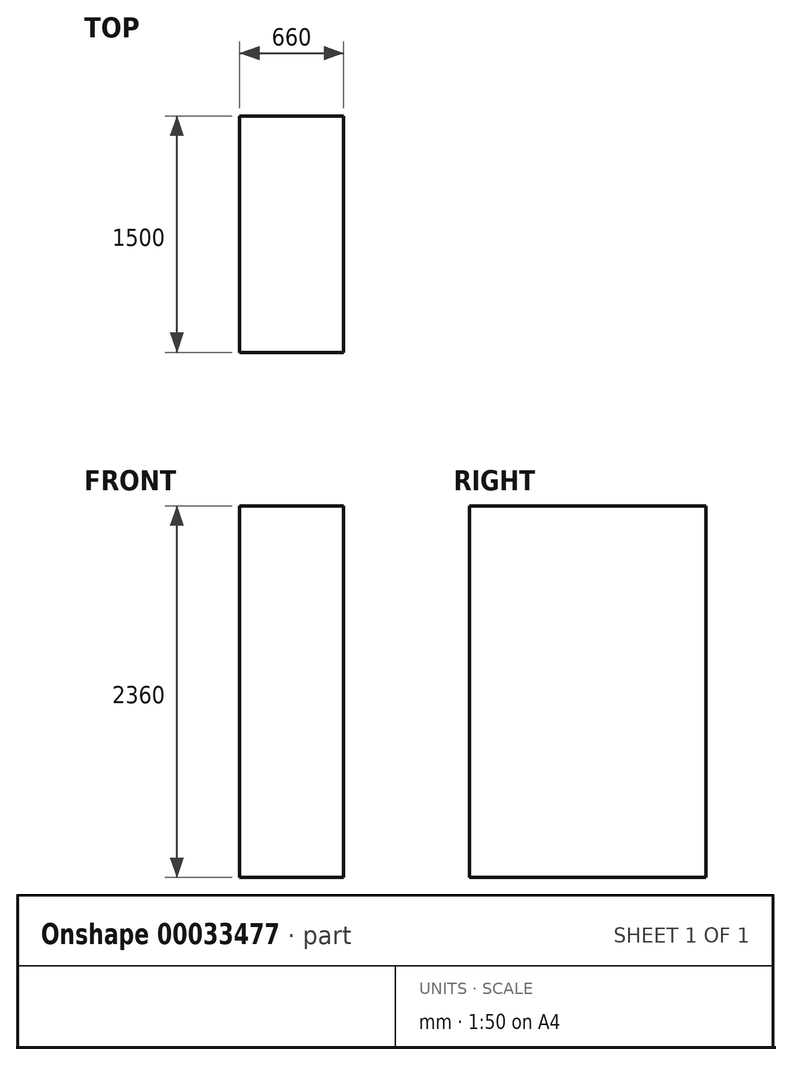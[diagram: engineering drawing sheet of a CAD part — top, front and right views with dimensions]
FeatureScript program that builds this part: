
annotation { "Feature Type Name" : "Feature", "Feature Type Description" : "" }
export const myFeature = defineFeature(function(context is Context, id is Id, definition is map)
    precondition{}
    {
        {
            var Q0;
            Q0=qCreatedBy(makeId("Top.planeOp"),FACE);
            var sketch = newSketch(context, id + "F0", { "sketchPlane" : qUnion([Q0])});
            skLineSegment(sketch, "E0.bottom", {"start": v(-329.17, 953.02) * mm, "end": v(330.83, 953.02) * mm});
            skLineSegment(sketch, "E0.top", {"start": v(-329.17, -546.98) * mm, "end": v(330.83, -546.98) * mm});
            skLineSegment(sketch, "E0.left", {"start": v(-329.17, 953.02) * mm, "end": v(-329.17, -546.98) * mm});
            skLineSegment(sketch, "E0.right", {"start": v(330.83, 953.02) * mm, "end": v(330.83, -546.98) * mm});
            skSolve(sketch);
        }
        {
            var Q0;
            Q0=makeQuery(id+"F0.imprint","IMPRINT",FACE,{"disambiguationData":[TD([[makeQuery(id+"F0.imprint","IMPRINT",EDGE,{"derivedFrom":sQuery(id+"F0.wireOp",EDGE,"E0.bottom")}),-1.0]])]});
            extrude(context, id + "F1", {"entities" : qUnion([Q0]), "depth" : 2360 * mm});
        }
    });
